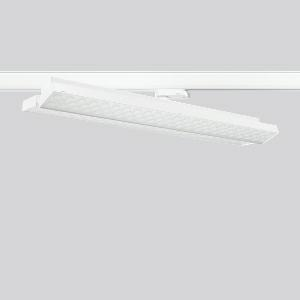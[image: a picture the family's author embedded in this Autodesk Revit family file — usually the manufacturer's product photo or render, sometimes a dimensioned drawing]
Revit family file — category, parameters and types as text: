
# Revit family: tx-move_742161_002_f608
name_source: partatom
category: Lighting Fixtures
units: mm (PartAtom-declared; Revit-internal decimal feet)

## family parameters
Cut with Voids When Loaded = No
Host = Face
Light Source = No
Part Type = Normal
Room Calculation Point = No
Round Connector Dimension = Use Diameter
Shared = No

## types (1)
- MultiLumen 1 (1 x LED Modul 830, 2900 lm, 3000)
    Apparent Load = 41 VA
    CIE Flux Codes = 90 97 99 100 100
    Color Rendering = 80
    Color Temperature = 3000
    Default Elevation = 1800 mm
    Description = Series: TX-MOVE
Multifunctional surface-mounted spotlight for area lighting. Very flat design. Housing: sheet steel, powder-coated. Rotation range: 356°. Swivel range: 90°. Consistent alignment possible with visible tilt scale. High-efficiency LED units with optimum light control thanks to clear plastic (PC) lens optics. Spezielle Mikrostrukturen reduzieren Gelbsaum. Symmetrical light distribution. With multi adaptor for 3-circuit tracks 230 V. Suitable for Track on ceiling. MultiLumen: Luminous flux adjustable in 3 steps. Factory setting is the highest luminous flux. Environmentally friendly and resource-saving due to replaceable and recyclable components. Very good glare control, ideal for till areas. 
Colour: traffic white, matt (RAL 9016)
Length: 570 mm
Width: 119 mm
Height: 92 mm
Lamp: LED
Socket: without socket
Colour temperature: 3000K
Colour rendering index (CRI): 80
System power: 41 W
Rated luminous flux: 5800 lm
Luminous efficiency: 141 lm/W
System power 2: 57 W
Rated luminous flux 2: 7850 lm
Luminous efficiency 2: 138 lm/W
System power 3: 73 W
Rated luminous flux 3: 9600 lm
Luminous efficiency 3: 132 lm/W
Control gear: Regulated power supply
Protection class: I
Type of protection: IP 20
    Height = 75 mm
    Lamp = 1 x LED Modul 830
    Lamp Light Flux = 2900 lm
    Lamp count = 1
    Length = 569 mm
    Lifetime = 50000 h
    Luminous efficacy = 141 lm/W
    Manufacturer = RZB
    ModVariant = No
    Model = 742161.002
    Mounting Place = Ceiling
    Mounting Type = Surface mounted
    Number of Poles = 1
    OnlyDefault = Yes
    Power Factor = 1
    Product Name = TX-MOVE
    Product group = Track mounted projectors
    ProductGroupID = 301
    Protection Class = Protection class I
    Protection Degree = IP 20
    RLX_Detail_Level = 1
    RLX_Emergency_Light_Flux = 0 lm
    RLX_Emergency_Type = 0
    RLX_Emergency_Type_DB = No
    RlxData = <blob elided: 31245 chars, md5=e47bbfd5>
    Socket = socket
    Standby Power = 0 W
    System Light Flux = 5800 lm
    System Power = 41 W
    Type Comments = MultiLumen 1
    Type Image = 742162.002.jpg
    URL = http://relux.com
    VarID = multilumen_1
    Voltage = 0 V
    Weight = 0.00 kg
    Width = 119 mm

## geometry (parser evidence)
native form markers: Blend x4, Sweep x14
no freeform markers — native parametric forms only
